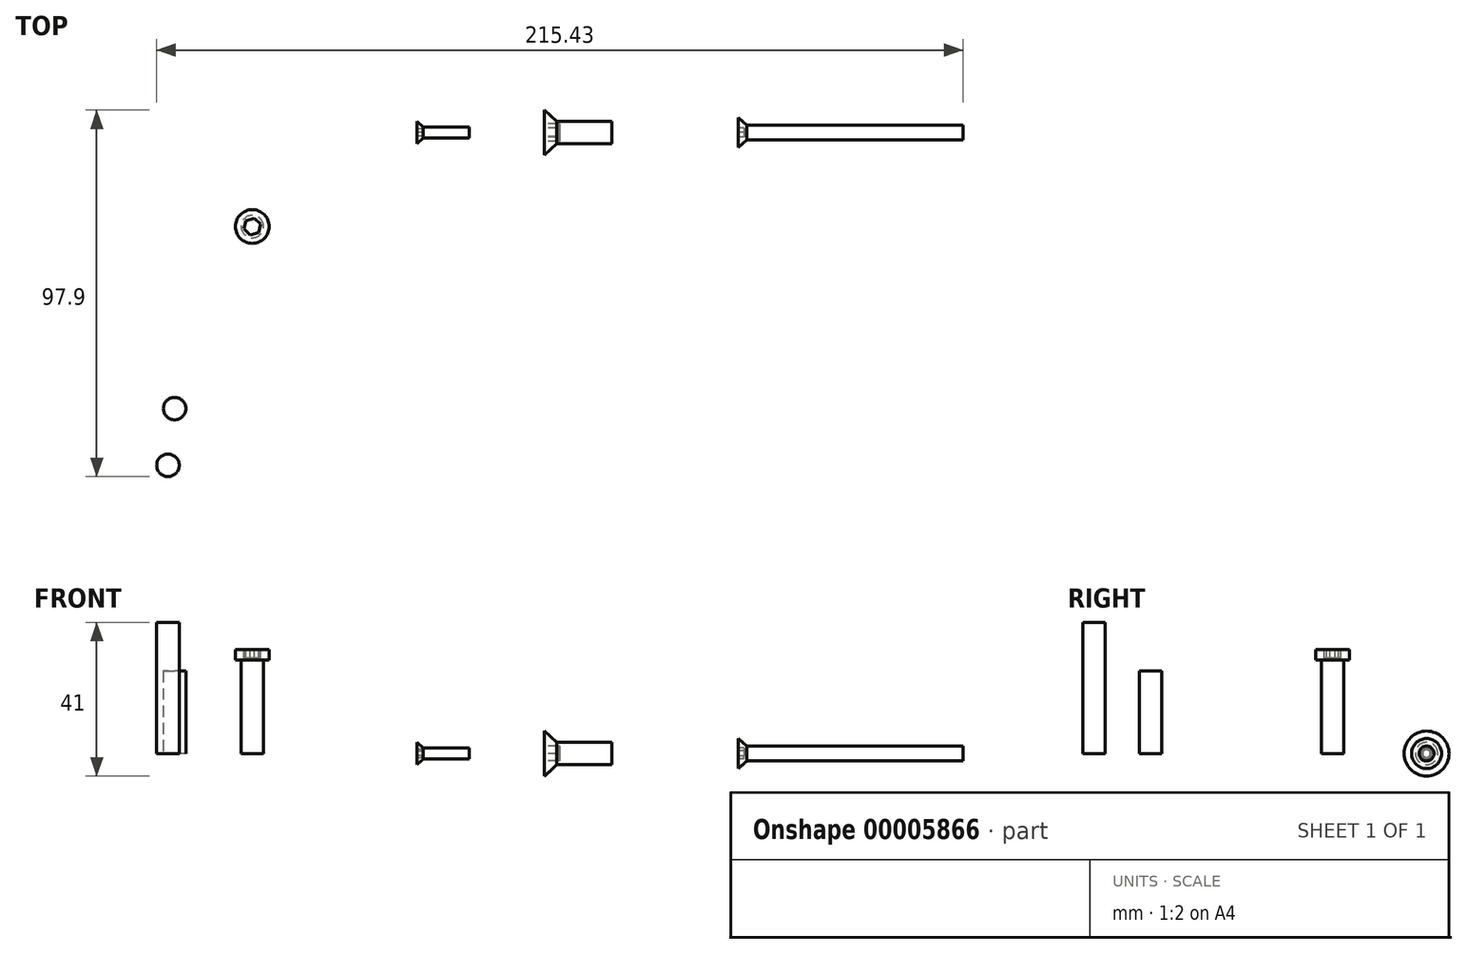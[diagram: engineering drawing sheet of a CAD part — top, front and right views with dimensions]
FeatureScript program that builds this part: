
annotation { "Feature Type Name" : "Feature", "Feature Type Description" : "" }
export const myFeature = defineFeature(function(context is Context, id is Id, definition is map)
    precondition{}
    {
        {
            var Q0;
            Q0=qCreatedBy(makeId("Top.planeOp"),FACE);
            var sketch = newSketch(context, id + "F0", { "sketchPlane" : qUnion([Q0])});
            skCircle(sketch, "E0", {"center": v(0, 0) * mm, "radius": 20 * mm, "construction": true});
            skLineSegment(sketch, "E1", {"start": v(0, 0) * mm, "end": v(41.2, 23.78) * mm, "construction": true});
            skLineSegment(sketch, "E2", {"start": v(0, 0) * mm, "end": v(-38.72, 22.35) * mm, "construction": true});
            skLineSegment(sketch, "E3", {"start": v(0, 0) * mm, "end": v(0, -44.81) * mm, "construction": true});
            skCircle(sketch, "E4", {"center": v(0, 0) * mm, "radius": 8.5 * mm});
            skLineSegment(sketch, "E5", {"start": v(0, 0) * mm, "end": v(0, 47.74) * mm, "construction": true});
            skLineSegment(sketch, "E6", {"start": v(0, 0) * mm, "end": v(63.8, -36.84) * mm, "construction": true});
            skLineSegment(sketch, "E7", {"start": v(0, 0) * mm, "end": v(-40.76, -23.53) * mm, "construction": true});
            skCircle(sketch, "E8", {"center": v(0, 0) * mm, "radius": 16.5 * mm, "construction": true});
            skArc(sketch, "E9", {"start": v(-12.56, 10.7) * mm, "mid": v(-16.89, 9.75) * mm, "end": v(-15.55, 5.53) * mm});
            skArc(sketch, "E10", {"start": v(15.55, 5.53) * mm, "mid": v(16.89, 9.75) * mm, "end": v(12.56, 10.7) * mm});
            skArc(sketch, "E11", {"start": v(-2.99, -16.23) * mm, "mid": v(0, -19.5) * mm, "end": v(2.99, -16.23) * mm});
            skArc(sketch, "E12", {"start": v(15.55, 5.53) * mm, "mid": v(7.6, -4.38) * mm, "end": v(2.99, -16.23) * mm});
            skArc(sketch, "E13", {"start": v(-12.56, 10.7) * mm, "mid": v(0, 8.84) * mm, "end": v(12.56, 10.7) * mm});
            skArc(sketch, "E14", {"start": v(-2.99, -16.23) * mm, "mid": v(-7.59, -4.38) * mm, "end": v(-15.55, 5.53) * mm});
            skSolve(sketch);
        }
        {
            var Q0;
            Q0 = qSketchRegion(id + "F0", true);
            var Q1;
            Q1=makeQuery(id+"F0.imprint","IMPRINT",FACE,{"disambiguationData":[TD([[makeQuery(id+"F0.imprint","IMPRINT",EDGE,{"derivedFrom":sQuery(id+"F0.wireOp",EDGE,"E4")}),1.0]])]});
            extrude(context, id + "F1", {"entities" : qUnion([Q0, Q1]), "depth" : 12.9 * mm});
        }
        {
            var Q0;
            Q0=qCreatedBy(makeId("Right.planeOp"),FACE);
            var sketch = newSketch(context, id + "F2", { "sketchPlane" : qUnion([Q0])});
            skArc(sketch, "E15", {"start": v(0, 12.95) * mm, "mid": v(-11.93, 11.76) * mm, "end": v(-23.14, 7.53) * mm});
            skLineSegment(sketch, "E16", {"start": v(-23.14, 7.53) * mm, "end": v(-23.14, 21.72) * mm});
            skLineSegment(sketch, "E17", {"start": v(-23.14, 21.72) * mm, "end": v(0, 21.72) * mm});
            skLineSegment(sketch, "E18", {"start": v(0, 21.72) * mm, "end": v(0, 12.95) * mm});
            skSolve(sketch);
        }
        {
            var Q0;
            Q0=makeQuery(id+"F2.imprint","IMPRINT",FACE,{"disambiguationData":[TD([[makeQuery(id+"F2.imprint","IMPRINT",EDGE,{"derivedFrom":sQuery(id+"F2.wireOp",EDGE,"E15")}),-1.0]])]});
            var Q1;
            Q1=sQuery(id+"F2.wireOp",EDGE,"E18");
            revolve(context, id + "F3", {"operationType" : NewBodyOperationType.REMOVE, "entities" : qUnion([Q0]), "axis" : qUnion([Q1]), "revolveType" : RevolveType.FULL, "oppositeDirection" : true});
        }
        {
            var Q0;
            Q0=makeQuery(id+"F1.opExtrude","CAP_FACE",FACE,{"disambiguationData":[OSD([sQuery(id+"F0.wireOp",EDGE,"E9"),sQuery(id+"F0.wireOp",EDGE,"E10"),sQuery(id+"F0.wireOp",EDGE,"E11"),sQuery(id+"F0.wireOp",EDGE,"E12"),sQuery(id+"F0.wireOp",EDGE,"E13"),sQuery(id+"F0.wireOp",EDGE,"E14")])],"isStart":true});
            var sketch = newSketch(context, id + "F4", { "sketchPlane" : qUnion([Q0])});
            skCircle(sketch, "E19", {"center": v(0, 0) * mm, "radius": 7.5 * mm});
            skSolve(sketch);
        }
        {
            var Q0;
            Q0=makeQuery(id+"F4.imprint","IMPRINT",FACE,{"disambiguationData":[TD([[makeQuery(id+"F4.imprint","IMPRINT",EDGE,{"derivedFrom":sQuery(id+"F4.wireOp",EDGE,"E19")}),1.0]])]});
            extrude(context, id + "F5", {"entities" : qUnion([Q0]), "operationType" : NewBodyOperationType.ADD, "depth" : 2 * mm});
        }
        {
            var Q0;
            Q0=makeQuery(id+"F5.opExtrude","CAP_FACE",FACE,{"disambiguationData":[OSD([sQuery(id+"F4.wireOp",EDGE,"E19")])],"isStart":false});
            var sketch = newSketch(context, id + "F6", { "sketchPlane" : qUnion([Q0])});
            skCircle(sketch, "E20", {"center": v(0, 0) * mm, "radius": 3 * mm});
            skSolve(sketch);
        }
        {
            var Q0;
            Q0 = qSketchRegion(id + "F6", true);
            extrude(context, id + "F7", {"entities" : qUnion([Q0]), "operationType" : NewBodyOperationType.REMOVE, "oppositeDirection" : true, "depth" : 6 * mm});
        }
        {
            var Q0;
            Q0=qCreatedBy(makeId("Top.planeOp"),FACE);
            var sketch = newSketch(context, id + "F8", { "sketchPlane" : qUnion([Q0])});
            skCircle(sketch, "E21", {"center": v(-103.93, -88.9) * mm, "radius": 3 * mm});
            skCircle(sketch, "E22", {"center": v(-102.15, -73.76) * mm, "radius": 3 * mm});
            skSolve(sketch);
        }
        {
            var Q0;
            Q0=makeQuery(id+"F8.imprint","IMPRINT",FACE,{"disambiguationData":[TD([[makeQuery(id+"F8.imprint","IMPRINT",EDGE,{"derivedFrom":sQuery(id+"F8.wireOp",EDGE,"E21")}),1.0]])]});
            extrude(context, id + "F9", {"entities" : qUnion([Q0]), "depth" : 35 * mm});
        }
        {
            var Q0;
            Q0=makeQuery(id+"F8.imprint","IMPRINT",FACE,{"disambiguationData":[TD([[makeQuery(id+"F8.imprint","IMPRINT",EDGE,{"derivedFrom":sQuery(id+"F8.wireOp",EDGE,"E22")}),1.0]])]});
            extrude(context, id + "F10", {"entities" : qUnion([Q0]), "depth" : 22 * mm});
        }
        {
            var Q0;
            Q0=qCreatedBy(makeId("Top.planeOp"),FACE);
            var sketch = newSketch(context, id + "F11", { "sketchPlane" : qUnion([Q0])});
            skCircle(sketch, "E23", {"center": v(-81.39, -25.13) * mm, "radius": 3 * mm});
            skSolve(sketch);
        }
        {
            var Q0;
            Q0 = qSketchRegion(id + "F11", true);
            extrude(context, id + "F12", {"entities" : qUnion([Q0]), "depth" : 25 * mm});
        }
        {
            var Q0;
            Q0=makeQuery(id+"F12.opExtrude","CAP_FACE",FACE,{"disambiguationData":[OSD([sQuery(id+"F11.wireOp",EDGE,"E23")])],"isStart":false});
            var sketch = newSketch(context, id + "F13", { "sketchPlane" : qUnion([Q0])});
            skCircle(sketch, "E24.0", {"center": v(-81.39, -25.13) * mm, "radius": 4.5 * mm});
            skSolve(sketch);
        }
        {
            var Q0;
            Q0 = qSketchRegion(id + "F13", true);
            extrude(context, id + "F14", {"entities" : qUnion([Q0]), "operationType" : NewBodyOperationType.ADD, "depth" : 2.8 * mm});
        }
        {
            var Q0;
            Q0=makeQuery(id+"F14.opExtrude","CAP_FACE",FACE,{"disambiguationData":[OSD([sQuery(id+"F13.wireOp",EDGE,"E24.0")])],"isStart":false});
            var sketch = newSketch(context, id + "F15", { "sketchPlane" : qUnion([Q0])});
            skCircle(sketch, "E25.0", {"center": v(-81.39, -25.13) * mm, "radius": 4.5 * mm});
            skCircle(sketch, "E26.cCircle", {"center": v(-81.39, -25.13) * mm, "radius": 2 * mm, "construction": true});
            skLineSegment(sketch, "E26.0", {"start": v(-80.85, -22.88) * mm, "end": v(-79.17, -24.47) * mm});
            skLineSegment(sketch, "E26.1", {"start": v(-79.17, -24.47) * mm, "end": v(-79.71, -26.72) * mm});
            skLineSegment(sketch, "E26.2", {"start": v(-79.71, -26.72) * mm, "end": v(-81.93, -27.37) * mm});
            skLineSegment(sketch, "E26.3", {"start": v(-81.93, -27.37) * mm, "end": v(-83.6, -25.78) * mm});
            skLineSegment(sketch, "E26.4", {"start": v(-83.6, -25.78) * mm, "end": v(-83.06, -23.54) * mm});
            skLineSegment(sketch, "E26.5", {"start": v(-83.06, -23.54) * mm, "end": v(-80.85, -22.88) * mm});
            skPoint(sketch, "E26.0.midPoint", {"position": v(-80, -23.68) * mm});
            skSolve(sketch);
        }
        {
            var Q0;
            Q0=makeQuery(id+"F15.imprint","IMPRINT",FACE,{"disambiguationData":[TD([[makeQuery(id+"F15.imprint","IMPRINT",EDGE,{"derivedFrom":sQuery(id+"F15.wireOp",EDGE,"E26.0")}),-1.0]])]});
            extrude(context, id + "F16", {"entities" : qUnion([Q0]), "operationType" : NewBodyOperationType.REMOVE, "oppositeDirection" : true, "depth" : 2.3 * mm});
        }
        {
            var Q0;
            Q0=qCreatedBy(makeId("Front.planeOp"),FACE);
            var sketch = newSketch(context, id + "F17", { "sketchPlane" : qUnion([Q0])});
            skLineSegment(sketch, "E27", {"start": v(-37.44, 0) * mm, "end": v(-37.44, 3) * mm});
            skLineSegment(sketch, "E28", {"start": v(-37.44, 3) * mm, "end": v(-35.74, 1.5) * mm});
            skLineSegment(sketch, "E29", {"start": v(-35.74, 1.5) * mm, "end": v(-23.44, 1.5) * mm});
            skLineSegment(sketch, "E30", {"start": v(-23.44, 1.5) * mm, "end": v(-23.44, 0) * mm});
            skLineSegment(sketch, "E31", {"start": v(-23.44, 0) * mm, "end": v(-37.44, 0) * mm});
            skLineSegment(sketch, "E32", {"start": v(-35.74, 1.5) * mm, "end": v(-37.44, 1.5) * mm});
            skSolve(sketch);
        }
        {
            var Q0;
            Q0 = qSketchRegion(id + "F17", true);
            var Q1;
            Q1=sQuery(id+"F17.wireOp",EDGE,"E31");
            revolve(context, id + "F18", {"entities" : qUnion([Q0]), "axis" : qUnion([Q1]), "revolveType" : RevolveType.FULL});
        }
        {
            var Q0;
            Q0=makeQuery(id+"F18.opRevolve","SWEPT_FACE",FACE,{"disambiguationData":[OSD([sQuery(id+"F17.wireOp",EDGE,"E27")])]});
            var sketch = newSketch(context, id + "F19", { "sketchPlane" : qUnion([Q0])});
            skCircle(sketch, "E33.cCircle", {"center": v(0, 0) * mm, "radius": 1 * mm, "construction": true});
            skLineSegment(sketch, "E33.0", {"start": v(1, 0.58) * mm, "end": v(1, -0.58) * mm});
            skLineSegment(sketch, "E33.1", {"start": v(1, -0.58) * mm, "end": v(0, -1.15) * mm});
            skLineSegment(sketch, "E33.2", {"start": v(0, -1.15) * mm, "end": v(-1, -0.58) * mm});
            skLineSegment(sketch, "E33.3", {"start": v(-1, -0.58) * mm, "end": v(-1, 0.58) * mm});
            skLineSegment(sketch, "E33.4", {"start": v(-1, 0.58) * mm, "end": v(0, 1.15) * mm});
            skLineSegment(sketch, "E33.5", {"start": v(0, 1.15) * mm, "end": v(1, 0.58) * mm});
            skPoint(sketch, "E33.0.midPoint", {"position": v(1, 0) * mm});
            skSolve(sketch);
        }
        {
            var Q0;
            Q0 = qSketchRegion(id + "F19", true);
            extrude(context, id + "F20", {"entities" : qUnion([Q0]), "operationType" : NewBodyOperationType.REMOVE, "oppositeDirection" : true, "depth" : 1.5 * mm});
        }
        {
            var Q0;
            Q0=makeQuery(id+"F1.opExtrude","SWEPT_BODY",BODY,{"disambiguationData":[OSD([sQuery(id+"F0.wireOp",EDGE,"E9"),sQuery(id+"F0.wireOp",EDGE,"E10"),sQuery(id+"F0.wireOp",EDGE,"E11"),sQuery(id+"F0.wireOp",EDGE,"E12"),sQuery(id+"F0.wireOp",EDGE,"E13"),sQuery(id+"F0.wireOp",EDGE,"E14")])]});
            deleteBodies(context, id + "F21", {"entities" : qUnion([Q0])});
        }
        {
            var Q0;
            Q0=qCreatedBy(makeId("Front.planeOp"),FACE);
            var sketch = newSketch(context, id + "F22", { "sketchPlane" : qUnion([Q0])});
            skLineSegment(sketch, "E34", {"start": v(48.5, 0) * mm, "end": v(48.5, 4) * mm});
            skLineSegment(sketch, "E35", {"start": v(48.5, 4) * mm, "end": v(50.8, 2) * mm});
            skLineSegment(sketch, "E36", {"start": v(50.8, 2) * mm, "end": v(108.5, 2) * mm});
            skLineSegment(sketch, "E37", {"start": v(108.5, 2) * mm, "end": v(108.5, 0) * mm});
            skLineSegment(sketch, "E38", {"start": v(108.5, 0) * mm, "end": v(48.5, 0) * mm});
            skSolve(sketch);
        }
        {
            var Q0;
            Q0 = qSketchRegion(id + "F22", true);
            var Q1;
            Q1=sQuery(id+"F22.wireOp",EDGE,"E38");
            revolve(context, id + "F23", {"entities" : qUnion([Q0]), "axis" : qUnion([Q1]), "revolveType" : RevolveType.FULL});
        }
        {
            var Q0;
            Q0=makeQuery(id+"F23.opRevolve","SWEPT_FACE",FACE,{"disambiguationData":[OSD([sQuery(id+"F22.wireOp",EDGE,"E34")])]});
            var sketch = newSketch(context, id + "F24", { "sketchPlane" : qUnion([Q0])});
            skCircle(sketch, "E39.cCircle", {"center": v(0, 0) * mm, "radius": 1.25 * mm, "construction": true});
            skLineSegment(sketch, "E39.0", {"start": v(1.25, 0.72) * mm, "end": v(1.25, -0.72) * mm});
            skLineSegment(sketch, "E39.1", {"start": v(1.25, -0.72) * mm, "end": v(0, -1.44) * mm});
            skLineSegment(sketch, "E39.2", {"start": v(0, -1.44) * mm, "end": v(-1.25, -0.72) * mm});
            skLineSegment(sketch, "E39.3", {"start": v(-1.25, -0.72) * mm, "end": v(-1.25, 0.72) * mm});
            skLineSegment(sketch, "E39.4", {"start": v(-1.25, 0.72) * mm, "end": v(0, 1.44) * mm});
            skLineSegment(sketch, "E39.5", {"start": v(0, 1.44) * mm, "end": v(1.25, 0.72) * mm});
            skPoint(sketch, "E39.0.midPoint", {"position": v(1.25, 0) * mm});
            skSolve(sketch);
        }
        {
            var Q0;
            Q0 = qSketchRegion(id + "F24", true);
            extrude(context, id + "F25", {"entities" : qUnion([Q0]), "operationType" : NewBodyOperationType.REMOVE, "oppositeDirection" : true, "depth" : 1.5 * mm});
        }
        {
            var Q0;
            Q0=qCreatedBy(makeId("Front.planeOp"),FACE);
            var sketch = newSketch(context, id + "F26", { "sketchPlane" : qUnion([Q0])});
            skLineSegment(sketch, "E40", {"start": v(-3.3, 0) * mm, "end": v(-3.3, 6) * mm});
            skLineSegment(sketch, "E41", {"start": v(-3.3, 6) * mm, "end": v(0, 3) * mm});
            skLineSegment(sketch, "E42", {"start": v(0, 3) * mm, "end": v(14.7, 3) * mm});
            skLineSegment(sketch, "E43", {"start": v(14.7, 3) * mm, "end": v(14.7, 0) * mm});
            skLineSegment(sketch, "E44", {"start": v(14.7, 0) * mm, "end": v(-3.3, 0) * mm});
            skSolve(sketch);
        }
        {
            var Q0;
            Q0 = qSketchRegion(id + "F26", true);
            var Q1;
            Q1=sQuery(id+"F26.wireOp",EDGE,"E44");
            revolve(context, id + "F27", {"entities" : qUnion([Q0]), "axis" : qUnion([Q1]), "revolveType" : RevolveType.FULL});
        }
        {
            var Q0;
            Q0=makeQuery(id+"F27.opRevolve","SWEPT_FACE",FACE,{"disambiguationData":[OSD([sQuery(id+"F26.wireOp",EDGE,"E40")])]});
            var sketch = newSketch(context, id + "F28", { "sketchPlane" : qUnion([Q0])});
            skCircle(sketch, "E45.cCircle", {"center": v(0, 0) * mm, "radius": 2 * mm, "construction": true});
            skLineSegment(sketch, "E45.0", {"start": v(2.3, 0) * mm, "end": v(1.16, -2) * mm});
            skLineSegment(sketch, "E45.1", {"start": v(1.16, -2) * mm, "end": v(-1.15, -2) * mm});
            skLineSegment(sketch, "E45.2", {"start": v(-1.15, -2) * mm, "end": v(-2.3, 0) * mm});
            skLineSegment(sketch, "E45.3", {"start": v(-2.3, 0) * mm, "end": v(-1.16, 2) * mm});
            skLineSegment(sketch, "E45.4", {"start": v(-1.16, 2) * mm, "end": v(1.15, 2) * mm});
            skLineSegment(sketch, "E45.5", {"start": v(1.15, 2) * mm, "end": v(2.3, 0) * mm});
            skPoint(sketch, "E45.0.midPoint", {"position": v(1.73, -1) * mm});
            skSolve(sketch);
        }
        {
            var Q0;
            Q0 = qSketchRegion(id + "F28", true);
            extrude(context, id + "F29", {"entities" : qUnion([Q0]), "operationType" : NewBodyOperationType.REMOVE, "oppositeDirection" : true, "depth" : 4 * mm});
        }
    });
